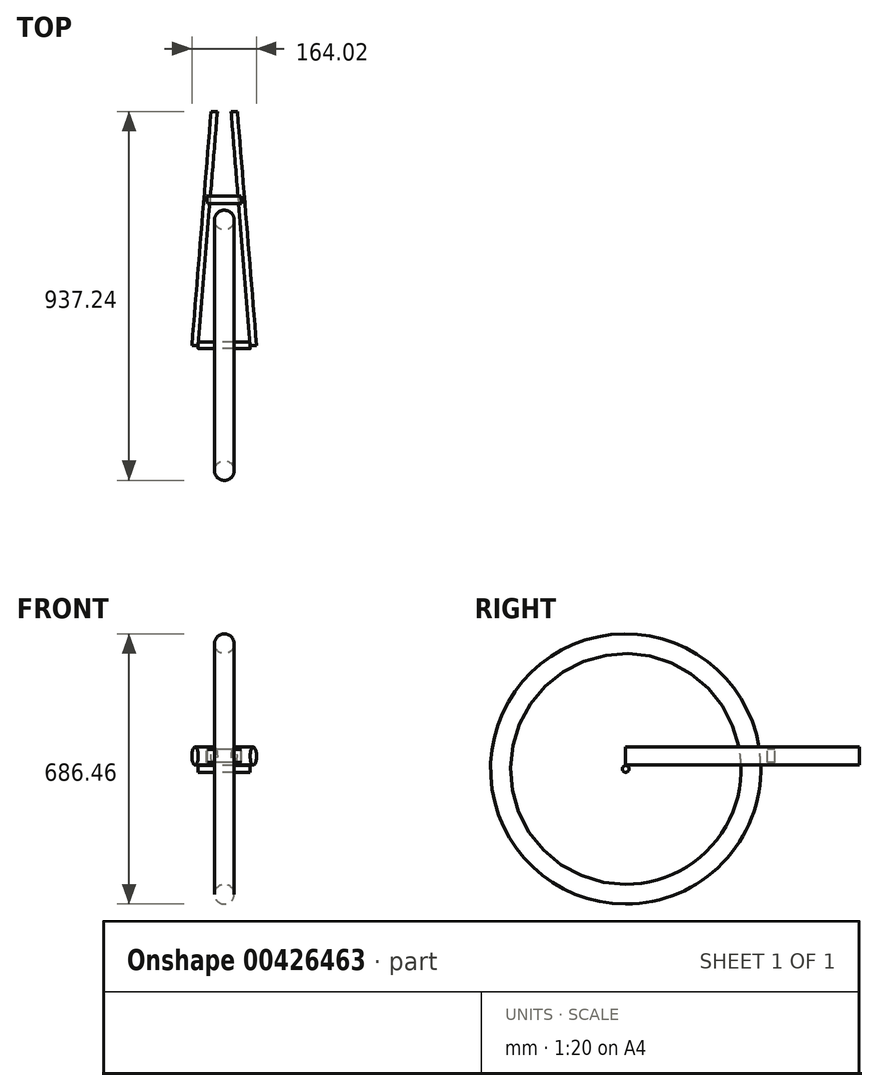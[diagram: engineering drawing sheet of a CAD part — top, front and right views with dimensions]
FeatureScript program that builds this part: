
annotation { "Feature Type Name" : "Feature", "Feature Type Description" : "" }
export const myFeature = defineFeature(function(context is Context, id is Id, definition is map)
    precondition{}
    {
        {
            var Q0;
            Q0=qCreatedBy(makeId("Right.planeOp"),FACE);
            var sketch = newSketch(context, id + "F0", { "sketchPlane" : qUnion([Q0])});
            skCircle(sketch, "E0", {"center": v(0, 0) * mm, "radius": 5 * mm});
            skSolve(sketch);
        }
        {
            var Q0;
            Q0=qCreatedBy(makeId("Right.planeOp"),FACE);
            cPlane(context, id + "F1", {"entities" : qUnion([Q0]), "cplaneType" : CPlaneType.OFFSET, "offset" : 26 * mm, "width" : 150 * mm, "height" : 150 * mm});
        }
        {
            var Q0;
            Q0=qCreatedBy(makeId("Right.planeOp"),FACE);
            cPlane(context, id + "F2", {"entities" : qUnion([Q0]), "cplaneType" : CPlaneType.OFFSET, "offset" : 92 * mm, "width" : 150 * mm, "height" : 150 * mm});
        }
        {
            var Q0;
            Q0=qCreatedBy(makeId("Top.planeOp"),FACE);
            cPlane(context, id + "F3", {"entities" : qUnion([Q0]), "cplaneType" : CPlaneType.OFFSET, "offset" : 32.8 * mm, "width" : 150 * mm, "height" : 150 * mm});
        }
        {
            var Q0;
            Q0=qCreatedBy(id+"F1.planeOp",FACE);
            var sketch = newSketch(context, id + "F4", { "sketchPlane" : qUnion([Q0])});
            skCircle(sketch, "E1", {"center": v(0, 0) * mm, "radius": 8.5 * mm});
            skSolve(sketch);
        }
        {
            var Q0;
            Q0 = qSketchRegion(id + "F4", true);
            extrude(context, id + "F5", {"entities" : qUnion([Q0]), "depth" : 132 * mm});
        }
        {
            var Q0;
            Q0=sQuery(id+"F0.wireOp",EDGE,"E0");
            extrude(context, id + "F6", {"bodyType" : ToolBodyType.SURFACE, "surfaceEntities" : qUnion([Q0]), "depth" : 184 * mm});
        }
        {
            var Q0;
            Q0=qCreatedBy(id+"F2.planeOp",FACE);
            var sketch = newSketch(context, id + "F7", { "sketchPlane" : qUnion([Q0])});
            skCircle(sketch, "E2", {"center": v(0, 0) * mm, "radius": 318 * mm});
            skSolve(sketch);
        }
        {
            var Q0;
            Q0=qCreatedBy(makeId("Front.planeOp"),FACE);
            var sketch = newSketch(context, id + "F8", { "sketchPlane" : qUnion([Q0])});
            skCircle(sketch, "E3", {"center": v(92.34, 318.23) * mm, "radius": 25 * mm});
            skSolve(sketch);
        }
        {
            var Q0;
            Q0=makeQuery(id+"F8.imprint","IMPRINT",FACE,{"disambiguationData":[TD([[makeQuery(id+"F8.imprint","IMPRINT",EDGE,{"derivedFrom":sQuery(id+"F8.wireOp",EDGE,"E3")}),1.0]])]});
            var Q1;
            Q1=sQuery(id+"F7.wireOp",EDGE,"E2");
            sweep(context, id + "F9", {"profiles" : qUnion([Q0]), "path" : qUnion([Q1])});
        }
        {
            var Q0;
            Q0=qCreatedBy(id+"F3.planeOp",FACE);
            var sketch = newSketch(context, id + "F10", { "sketchPlane" : qUnion([Q0])});
            skLineSegment(sketch, "E4", {"start": v(166, 0) * mm, "end": v(117.35, 594.01) * mm});
            skSolve(sketch);
        }
        {
            var Q0;
            Q0=qCreatedBy(makeId("Front.planeOp"),FACE);
            var sketch = newSketch(context, id + "F11", { "sketchPlane" : qUnion([Q0])});
            skEllipse(sketch, "E5", {"center": v(166, 32.8) * mm, "majorRadius": 23 * mm, "minorRadius": 8 * mm, "majorAxis": v(0, -1)});
            skSolve(sketch);
        }
        {
            var Q0;
            Q0=makeQuery(id+"F11.imprint","IMPRINT",FACE,{"disambiguationData":[TD([[makeQuery(id+"F11.imprint","IMPRINT",EDGE,{"derivedFrom":sQuery(id+"F11.wireOp",EDGE,"E5")}),1.0]])]});
            var Q1;
            Q1=sQuery(id+"F10.wireOp",EDGE,"E4");
            sweep(context, id + "F12", {"profiles" : qUnion([Q0]), "path" : qUnion([Q1])});
        }
        {
            var Q0;
            Q0=makeQuery(id+"F12.opSweep","SWEPT_BODY",BODY,{"disambiguationData":[OSD([sQuery(id+"F10.wireOp",EDGE,"E4"),sQuery(id+"F11.wireOp",EDGE,"E5")])]});
            var Q1;
            Q1=qCreatedBy(id+"F2.planeOp",FACE);
            mirror(context, id + "F13", {"entities" : qUnion([Q0]), "mirrorPlane" : qUnion([Q1])});
        }
        {
            var Q0;
            Q0=qCreatedBy(id+"F3.planeOp",FACE);
            var sketch = newSketch(context, id + "F14", { "sketchPlane" : qUnion([Q0])});
            skLineSegment(sketch, "E6", {"start": v(48.04, 369.54) * mm, "end": v(135.3, 369.54) * mm});
            skSolve(sketch);
        }
        {
            var Q0;
            Q0 = qBodyType(qCreatedBy(id + "F10" ,EDGE), BodyType.WIRE);
            cPlane(context, id + "F15", {"entities" : qUnion([Q0]), "cplaneType" : CPlaneType.LINE_ANGLE, "offset" : 25 * mm, "angle" : 90 * degree, "width" : 150 * mm, "height" : 150 * mm});
        }
        {
            var Q0;
            Q0=qCreatedBy(id+"F15.planeOp",FACE);
            var sketch = newSketch(context, id + "F16", { "sketchPlane" : qUnion([Q0])});
            skLineSegment(sketch, "E7.bottom", {"start": v(367.37, 16.11) * mm, "end": v(347.16, 16.11) * mm});
            skLineSegment(sketch, "E7.top", {"start": v(367.37, 49.49) * mm, "end": v(347.16, 49.49) * mm});
            skLineSegment(sketch, "E7.left", {"start": v(367.37, 16.11) * mm, "end": v(367.37, 49.49) * mm});
            skLineSegment(sketch, "E7.right", {"start": v(347.16, 16.11) * mm, "end": v(347.16, 49.49) * mm});
            skPoint(sketch, "E7.middle", {"position": v(357.26, 32.8) * mm});
            skSolve(sketch);
        }
        {
            var Q0;
            Q0 = qSketchRegion(id + "F16", true);
            var Q1;
            Q1=sQuery(id+"F14.wireOp",EDGE,"E6");
            sweep(context, id + "F17", {"profiles" : qUnion([Q0]), "path" : qUnion([Q1])});
        }
    });
